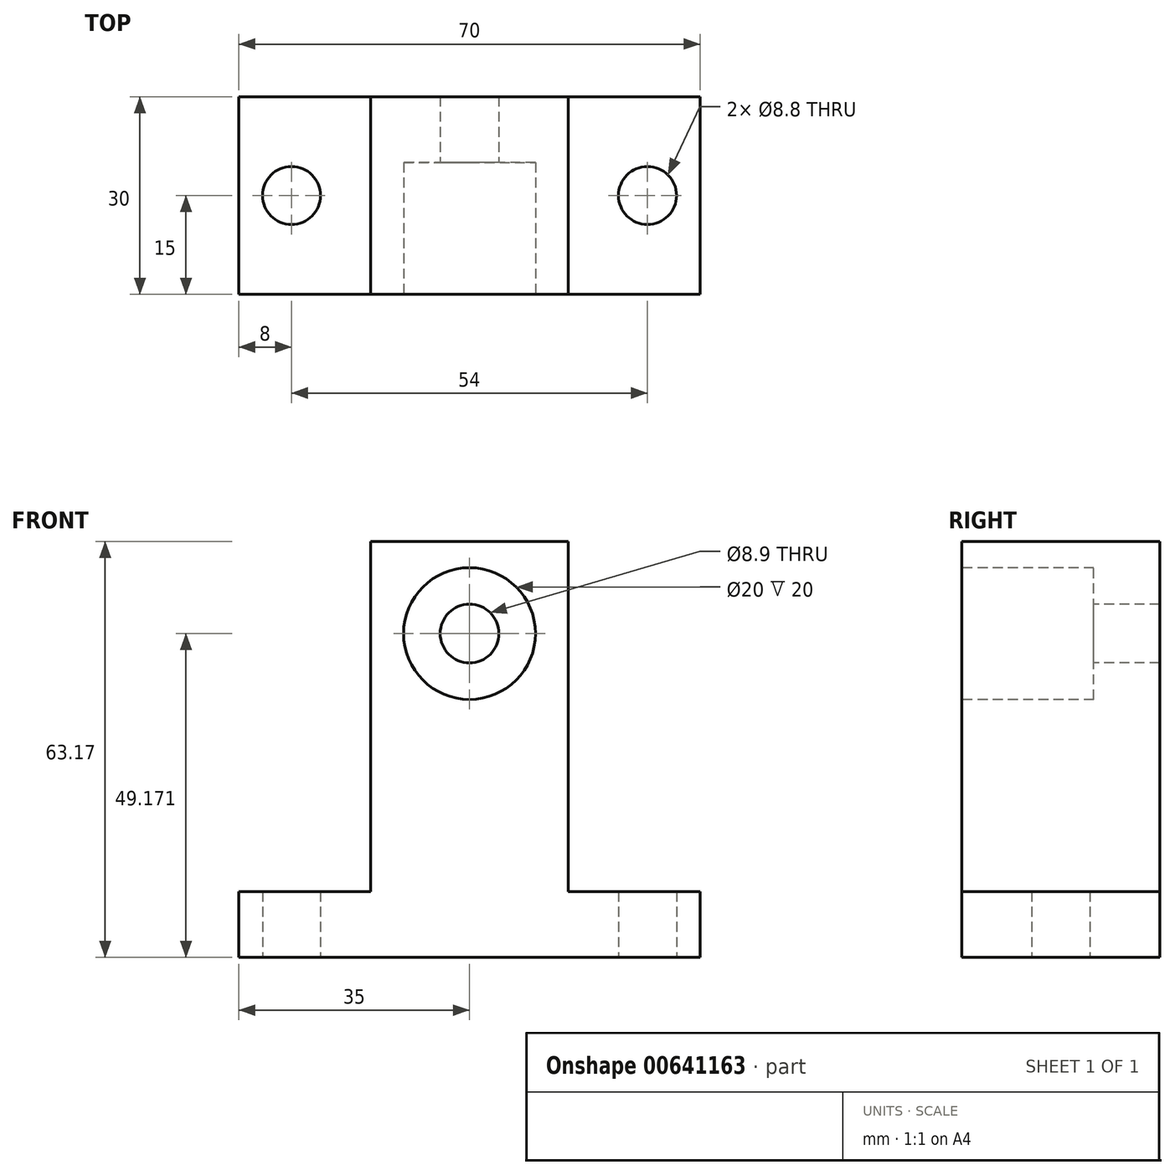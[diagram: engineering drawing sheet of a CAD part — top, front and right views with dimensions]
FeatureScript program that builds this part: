
annotation { "Feature Type Name" : "Feature", "Feature Type Description" : "" }
export const myFeature = defineFeature(function(context is Context, id is Id, definition is map)
    precondition{}
    {
        {
            var Q0;
            Q0=qCreatedBy(makeId("Front.planeOp"),FACE);
            var sketch = newSketch(context, id + "F0", { "sketchPlane" : qUnion([Q0])});
            skLineSegment(sketch, "E0", {"start": v(0, 0) * mm, "end": v(70, 0) * mm});
            skLineSegment(sketch, "E1", {"start": v(70, 0) * mm, "end": v(70, 10) * mm});
            skLineSegment(sketch, "E2", {"start": v(70, 10) * mm, "end": v(50, 10) * mm});
            skLineSegment(sketch, "E3", {"start": v(50, 10) * mm, "end": v(50, 63.17) * mm});
            skLineSegment(sketch, "E4", {"start": v(50, 63.17) * mm, "end": v(20, 63.17) * mm});
            skLineSegment(sketch, "E5", {"start": v(20, 63.17) * mm, "end": v(20, 10) * mm});
            skLineSegment(sketch, "E6", {"start": v(20, 10) * mm, "end": v(0, 10) * mm});
            skLineSegment(sketch, "E7", {"start": v(0, 10) * mm, "end": v(0, 0) * mm});
            skSolve(sketch);
        }
        {
            var Q0;
            Q0=makeQuery(id+"F0.imprint","IMPRINT",FACE,{"disambiguationData":[TD([[makeQuery(id+"F0.imprint","IMPRINT",EDGE,{"derivedFrom":sQuery(id+"F0.wireOp",EDGE,"E0")}),1.0]])]});
            extrude(context, id + "F1", {"entities" : qUnion([Q0]), "depth" : 30 * mm, "offsetDistance" : 25 * mm});
        }
        {
            var Q0;
            Q0=makeQuery(id+"F1.opExtrude","CAP_FACE",FACE,{"disambiguationData":[OSD([sQuery(id+"F0.wireOp",EDGE,"E0"),sQuery(id+"F0.wireOp",EDGE,"E1"),sQuery(id+"F0.wireOp",EDGE,"E2"),sQuery(id+"F0.wireOp",EDGE,"E3"),sQuery(id+"F0.wireOp",EDGE,"E4"),sQuery(id+"F0.wireOp",EDGE,"E5"),sQuery(id+"F0.wireOp",EDGE,"E6"),sQuery(id+"F0.wireOp",EDGE,"E7")])],"isStart":false});
            var sketch = newSketch(context, id + "F2", { "sketchPlane" : qUnion([Q0])});
            skPoint(sketch, "E8", {"position": v(35, 49.17) * mm});
            skPoint(sketch, "E8.positionSnap0", {"position": v(35, 63.17) * mm});
            skSolve(sketch);
        }
        {
            var Q0;
            Q0=sQuery(id+"F2.wireOp",VERTEX,"E8");
            var Q1;
            Q1=makeQuery(id+"F1.opExtrude","SWEPT_BODY",BODY,{"disambiguationData":[OSD([sQuery(id+"F0.wireOp",EDGE,"E0"),sQuery(id+"F0.wireOp",EDGE,"E1"),sQuery(id+"F0.wireOp",EDGE,"E2"),sQuery(id+"F0.wireOp",EDGE,"E3"),sQuery(id+"F0.wireOp",EDGE,"E4"),sQuery(id+"F0.wireOp",EDGE,"E5"),sQuery(id+"F0.wireOp",EDGE,"E6"),sQuery(id+"F0.wireOp",EDGE,"E7")])]});
            hole(context, id + "F3", {"style" : HoleStyle.C_BORE, "endStyle" : HoleEndStyle.THROUGH, "holeDiameter" : 8.9 * mm, "cBoreDiameter" : 20 * mm, "cBoreDepth" : 20 * mm, "majorDiameter" : 5 * mm, "isTappedThrough" : true, "tappedDepth" : 14.5 * mm, "tapClearance" : 3, "startFromSketch" : true, "locations" : qUnion([Q0]), "scope" : qUnion([Q1])});
        }
        {
            var Q0;
            Q0=makeQuery(id+"F1.opExtrude","SWEPT_FACE",FACE,{"disambiguationData":[OSD([sQuery(id+"F0.wireOp",EDGE,"E0")])]});
            var sketch = newSketch(context, id + "F4", { "sketchPlane" : qUnion([Q0])});
            skPoint(sketch, "E9", {"position": v(8, 15) * mm});
            skPoint(sketch, "E9.positionSnap0", {"position": v(0, 15) * mm});
            skPoint(sketch, "E10", {"position": v(70, 15) * mm});
            skPoint(sketch, "E11", {"position": v(62, 15) * mm});
            skSolve(sketch);
        }
        {
            var Q0;
            Q0=sQuery(id+"F4.wireOp",VERTEX,"E9");
            var Q1;
            Q1=sQuery(id+"F4.wireOp",VERTEX,"E11");
            var Q2;
            Q2=makeQuery(id+"F1.opExtrude","SWEPT_BODY",BODY,{"disambiguationData":[OSD([sQuery(id+"F0.wireOp",EDGE,"E0"),sQuery(id+"F0.wireOp",EDGE,"E1"),sQuery(id+"F0.wireOp",EDGE,"E2"),sQuery(id+"F0.wireOp",EDGE,"E3"),sQuery(id+"F0.wireOp",EDGE,"E4"),sQuery(id+"F0.wireOp",EDGE,"E5"),sQuery(id+"F0.wireOp",EDGE,"E6"),sQuery(id+"F0.wireOp",EDGE,"E7")])]});
            hole(context, id + "F5", {"style" : HoleStyle.SIMPLE, "endStyle" : HoleEndStyle.THROUGH, "standardTappedOrClearance" : lookupTablePath({ "standard" : "ISO", "fit" : "Normal", "size" : "M8", "type" : "Clearance" }), "standardBlindInLast" : lookupTablePath({ "fit" : "Standard", "standard" : "ISO", "size" : "M8", "type" : "Clearance" }), "holeDiameter" : 8.8 * mm, "majorDiameter" : 5 * mm, "isTappedThrough" : true, "tappedDepth" : 14.5 * mm, "tapClearance" : 3, "startFromSketch" : true, "locations" : qUnion([Q0, Q1]), "scope" : qUnion([Q2])});
        }
    });
